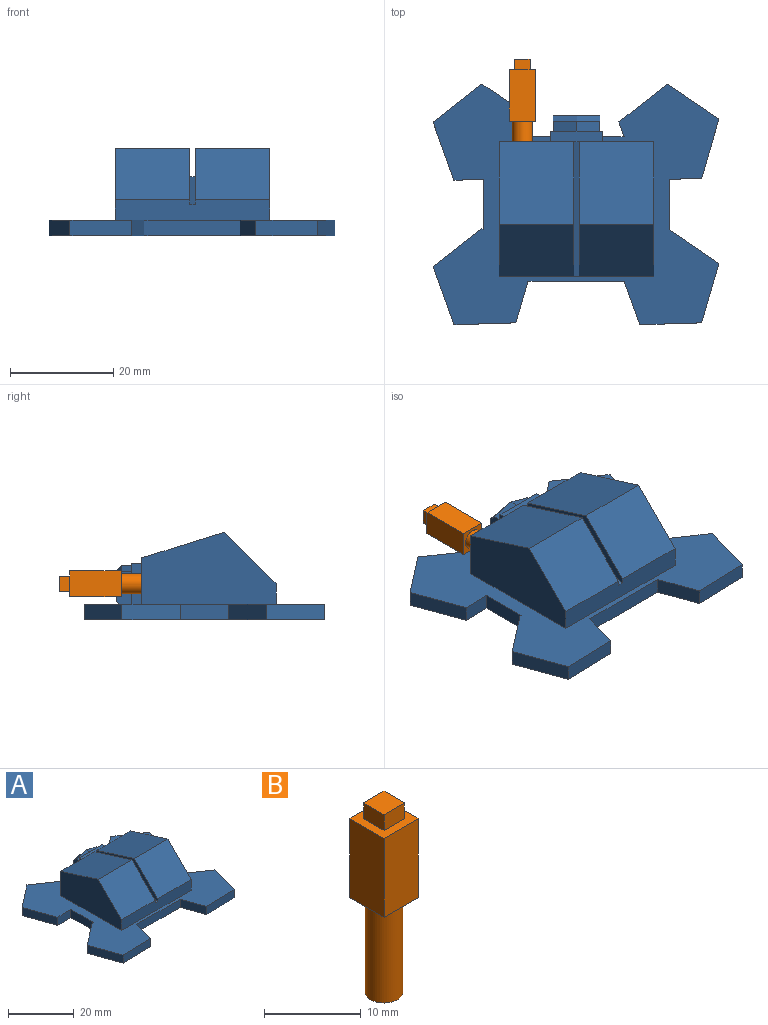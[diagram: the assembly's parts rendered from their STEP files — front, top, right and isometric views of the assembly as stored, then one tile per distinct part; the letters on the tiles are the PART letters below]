
ASSEMBLY  parts=2 mates=1
PART A: 61 faces, bbox 55.4x46.6x17 mm
  f0: plane 30x4mm, normal (0,-1,0), area 119.1mm2, adj f3,f7,f32,f33,f35,f58,f59,f60
  f1: plane 30x9mm, normal (0,1,0), area 164.3mm2, adj f2,f7,f32,f33,f34,f36,f37,f38
  f2: plane 16x14.5mm, normal (0,0.3,0.95), area 243.1mm2, adj f1,f3,f33,f59
  f3: plane 14.5x10mm, normal (0,-0.71,0.71), area 205.1mm2, adj f0,f2,f33,f59
  f4: plane 4.23x3mm, normal (0,1,0), area 12.7mm2, adj f7,f25,f31,f38
  f5: plane 9x5.97mm, normal (0,1,0), area 44.4mm2, adj f39,f42,f43,f44,f45,f46,f47,f49
  f6: plane 11x10mm, normal (0,1,0), area 25.4mm2, adj f31,f36,f37,f38,f39,f40,f41,f42
  f7: plane 55.41x46.64mm, normal (0,0,1), area 961.2mm2, adj f0,f1,f4,f8,f9,f10,f11,f12
  f8: plane 5.74x3mm, normal (0.03,-1,0), area 17.2mm2, adj f7,f9,f30,f31
  f9: plane 9.75x3mm, normal (-1,0,0), area 29.2mm2, adj f7,f8,f10,f31
  f10: plane 3x0.31mm, normal (0.56,0.83,0), area 1.1mm2, adj f7,f9,f11,f31
  f11: plane 9.49x7.35mm, normal (-0.61,0.79,0), area 36mm2, adj f7,f10,f12,f31
  f12: plane 11.29x4.06mm, normal (-0.94,-0.34,0), area 36mm2, adj f7,f11,f13,f31
  f13: plane 11.99x3mm, normal (0.03,-1,0), area 36mm2, adj f7,f12,f14,f31
  f14: plane 8.07x3mm, normal (0.96,-0.28,0), area 25.2mm2, adj f7,f13,f15,f31
  f15: plane 18.62x3mm, normal (0,-1,0), area 55.9mm2, adj f7,f14,f16,f31
  f16: plane 8.44x3.03mm, normal (-0.94,-0.34,0), area 26.9mm2, adj f7,f15,f17,f31
  f17: plane 11.99x3mm, normal (0.03,-1,0), area 36mm2, adj f7,f16,f18,f31
  f18: plane 11.52x3.36mm, normal (0.96,-0.28,0), area 36mm2, adj f7,f17,f19,f31
  f19: plane 9.61x6.54mm, normal (0.56,0.83,0), area 34.9mm2, adj f7,f18,f20,f31
  f20: plane 9.75x3mm, normal (1,0,0), area 29.2mm2, adj f7,f19,f21,f31
  f21: plane 6.25x3mm, normal (0.03,-1,0), area 18.8mm2, adj f7,f20,f22,f31
  f22: plane 11.52x3.36mm, normal (0.96,-0.28,0), area 36mm2, adj f7,f21,f23,f31
  f23: plane 9.92x6.75mm, normal (0.56,0.83,0), area 36mm2, adj f7,f22,f24,f31
  f24: plane 9.49x7.35mm, normal (-0.61,0.79,0), area 36mm2, adj f7,f23,f25,f31
  f25: plane 3x2.85mm, normal (-0.94,-0.34,0), area 9.1mm2, adj f4,f7,f24,f31
  f26: plane 4.4x3mm, normal (0,1,0), area 13.2mm2, adj f7,f27,f31,f36
  f27: plane 3.45x3mm, normal (0.96,-0.28,0), area 10.8mm2, adj f7,f26,f28,f31
  f28: plane 9.92x6.75mm, normal (0.56,0.83,0), area 36mm2, adj f7,f27,f29,f31
  f29: plane 9.49x7.35mm, normal (-0.61,0.79,0), area 36mm2, adj f7,f28,f30,f31
  f30: plane 11.29x4.06mm, normal (-0.94,-0.34,0), area 36mm2, adj f7,f8,f29,f31
  f31: plane 55.41x46.64mm, normal (0,0,-1), area 1761.2mm2, adj f4,f6,f8,f9,f10,f11,f12,f13
  f32: plane 26x14mm, normal (1,0,0), area 274mm2, adj f0,f1,f7,f34,f35
  f33: plane 26x14mm, normal (-1,0,0), area 274mm2, adj f0,f1,f2,f3,f7
  f34: plane 16x14.5mm, normal (0,0.3,0.95), area 243.1mm2, adj f1,f32,f35,f60
  f35: plane 14.5x10mm, normal (0,-0.71,0.71), area 205.1mm2, adj f0,f32,f34,f60
  f36: plane 11x2mm, normal (-1,0,0), area 19mm2, adj f1,f6,f7,f26,f31,f37
  f37: plane 10x2mm, normal (0,0,1), area 20mm2, adj f1,f6,f36,f38
  f38: plane 11x2mm, normal (1,0,0), area 19mm2, adj f1,f4,f6,f7,f31,f37
  f39: plane 8.8x3mm, normal (-1,0,0), area 21.4mm2, adj f5,f6,f40,f44,f57
  f40: plane 4.5x2mm, normal (-0.26,0,0.97), area 9.3mm2, adj f6,f39,f41,f44
  f41: plane 4.5x2mm, normal (0.26,0,0.97), area 9.3mm2, adj f6,f40,f42,f43
  f42: plane 8.8x3mm, normal (1,0,0), area 21.4mm2, adj f5,f6,f41,f43,f57
  f43: plane 4.5x2.24mm, normal (0.18,0.71,0.68), area 6.6mm2, adj f5,f41,f42,f44
  f44: plane 4.5x2.24mm, normal (-0.18,0.71,0.68), area 6.6mm2, adj f5,f39,f40,f43
  f45: plane 2.62x1.47mm, normal (0.49,0,-0.87), area 3mm2, adj f5,f46,f47,f48
  f46: plane 1.47x1mm, normal (-1,0,0), area 1.5mm2, adj f5,f45,f47,f48
  f47: plane 2.62x1mm, normal (0,0,1), area 2.6mm2, adj f5,f45,f46,f48
  f48: plane 2.62x1.47mm, normal (0,1,0), area 1.9mm2, adj f45,f46,f47
  f49: plane 2.62x1.47mm, normal (-0.49,0,-0.87), area 3mm2, adj f5,f50,f51,f52
  f50: plane 2.62x1mm, normal (0,0,1), area 2.6mm2, adj f5,f49,f51,f52
  f51: plane 1.47x1mm, normal (1,0,0), area 1.5mm2, adj f5,f49,f50,f52
  f52: plane 2.62x1.47mm, normal (0,1,0), area 1.9mm2, adj f49,f50,f51
  f53: cylinder r=2mm len=8mm, axis (0,1,0), area 100.5mm2, adj f1,f54
  f54: plane 4x4mm, normal (0,1,0), area 12.6mm2, adj f53
  f55: cylinder r=2mm len=8mm, axis (0,1,0), area 100.5mm2, adj f1,f56
  f56: plane 4x4mm, normal (0,1,0), area 12.6mm2, adj f55
  f57: plane 9x3mm, normal (0,0.71,-0.71), area 38.2mm2, adj f5,f6,f39,f42
  f58: plane 26x5.42mm, normal (0,-0.2,0.98), area 26.6mm2, adj f0,f1,f59,f60
  f59: plane 26x10.95mm, normal (1,0,0), area 124.2mm2, adj f0,f1,f2,f3,f58
  f60: plane 26x10.95mm, normal (-1,0,0), area 124.2mm2, adj f0,f1,f34,f35,f58
PART B: 13 faces, bbox 5x5x24 mm
  f0: plane 5x5mm, normal (0,0,1), area 16mm2, adj f3,f4,f5,f6,f8,f9,f10,f11
  f1: cylinder r=1.95mm len=12mm, axis (0,0,-1), area 147mm2, adj f2,f7
  f2: plane 3.9x3.9mm, normal (0,0,-1), area 11.9mm2, adj f1
  f3: plane 10x5mm, normal (0,-1,0), area 50mm2, adj f0,f4,f6,f7
  f4: plane 10x5mm, normal (1,0,0), area 50mm2, adj f0,f3,f5,f7
  f5: plane 10x5mm, normal (0,1,0), area 50mm2, adj f0,f4,f6,f7
  f6: plane 10x5mm, normal (-1,0,0), area 50mm2, adj f0,f3,f5,f7
  f7: plane 5x5mm, normal (0,0,-1), area 13.1mm2, adj f1,f3,f4,f5,f6
  f8: plane 3x2mm, normal (0,-1,0), area 6mm2, adj f0,f9,f11,f12
  f9: plane 3x2mm, normal (1,0,0), area 6mm2, adj f0,f8,f10,f12
  f10: plane 3x2mm, normal (0,1,0), area 6mm2, adj f0,f9,f11,f12
  f11: plane 3x2mm, normal (-1,0,0), area 6mm2, adj f0,f8,f10,f12
  f12: plane 3x3mm, normal (0,0,1), area 9mm2, adj f8,f9,f10,f11
PLACE A t=(-0.85,14.1,1.91)mm
PLACE B rot(axis=(-1,0,0),90deg) t=(-11.35,19.1,8.91)mm
MATE fastened A.f53 <-> B.f1  axis (0,1,0) through (-11.35,19.1,8.91)mm
